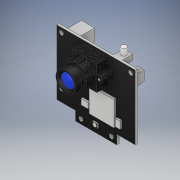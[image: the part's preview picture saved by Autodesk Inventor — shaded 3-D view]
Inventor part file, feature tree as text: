
AUTODESK INVENTOR PART (.ipt)
format: ipt  version: 2017 (Build 210142000, 142)  size: 648,704 bytes
history: native  units: in
note: dims shown in document units (in); Inventor stores cm internally (conversion verified against a paired STEP export)
features: sketch x25, extrude x23, projected_geometry x8, chamfer x5, pattern_linear x4, plane x2, revolve x2, fillet x2, mirror x1, other x1
ambient origin geometry x8: Origin, YZ Plane, XZ Plane, XY Plane, X Axis, Y Axis, Z Axis, Center Point
bodies: Solid1 (feature_tree)
feature tree (73):
  extrude  "Extrusion1"  Depth=1.75in
  extrude  "Extrusion2"  Depth=0.5in
  extrude  "Extrusion3"  Depth=0.25in
  extrude  "Extrusion4"  Depth=0.12in
  plane  "Work Plane1"
  revolve  "Revolution1"  [1 undecoded]
  extrude  "Extrusion5"  Depth=0.125in
  extrude  "Extrusion6"  Depth=0.15in
  extrude  "Extrusion7"  Depth=0.06in TaperAngle=0.0deg
  extrude  "Extrusion8"  Depth=0.175in
  extrude  "Extrusion9"  Depth=0.063in
  extrude  "Extrusion10"  Depth=0.06in
  plane  "Work Plane2"
  mirror  "Mirror1"
  extrude  "Extrusion11"  Depth=0.59in
  extrude  "Extrusion12"  Depth=0.0016in
  chamfer  "Chamfer1"  Distance=0.2598in
  extrude  "Extrusion13"  Depth=0.047in
  chamfer  "Chamfer2"  Distance=0.038in
  pattern_linear  "Rectangular Pattern1"  Spacing1=0.145in  [1 undecoded]
  extrude  "Extrusion14"  Depth=0.407in
  extrude  "Extrusion15"  Depth=0.284in TaperAngle=0.0deg
  fillet  "Fillet1"  Radius=0.1225in
  extrude  "Extrusion16"  Depth=0.127in
  chamfer  "Chamfer3"  Distance=0.135in
  pattern_linear  "Rectangular Pattern3"  Spacing1=0.173in  [1 undecoded]
  pattern_linear  "Rectangular Pattern4"  Spacing1=0.158in  [1 undecoded]
  extrude  "Extrusion17"  Depth=0.3in
  extrude  "Extrusion18"  Depth=0.369in TaperAngle=0.0deg
  chamfer  "Chamfer4"  Distance=0.018in
  pattern_linear  "Rectangular Pattern5"  Spacing1=0.0543in  [1 undecoded]
  extrude  "Extrusion19"  Depth=0.1in TaperAngle=0.0deg
  extrude  "Extrusion20"  Depth=0.35in
  fillet  "Fillet2"  Radius=0.8in
  extrude  "Extrusion21"  Depth=0.184in
  extrude  "Extrusion22"  Depth=0.049in
  revolve  "Revolution2"  [1 undecoded]
  extrude  "Extrusion23"  Depth=0.127in
  chamfer  "Chamfer5"  Distance=0.174in
  sketch  "Sketch1"  dims[d0=2.12in d1=1.75in]
  sketch  "Sketch2"  dims[d2=0.5in d3=0.5in]
  sketch  "Sketch3"  dims[d4=0.25in d5=0.125in]
  projected_geometry  "Projected Loop1"
  sketch  "Sketch4"  dims[d6=0.125in d7=0.12in]
  projected_geometry  "Projected Loop2"
  other  "Work Axis1"
  sketch  "Sketch5"  dims[d8=0.125in d9=0.12in]
  projected_geometry  "Projected Loop3"
  sketch  "Sketch6"  dims[d10=0.32in d11=0.125in]
  sketch  "Sketch7"  dims[d12=0.15in d13=0.15in]
  sketch  "Sketch8"  dims[d14=0.125in d15=0.06in d16=0.0in]
  sketch  "Sketch9"  dims[d17=0.67in d18=0.175in]
  sketch  "Sketch10"  dims[d19=0.964in d20=0.063in]
  sketch  "Sketch11"  dims[d21=0.06in d22=0.335in]
  projected_geometry  "Projected Loop4"
  sketch  "Sketch12"  dims[d23=0.314in d24=0.0in d25=0.59in]
  sketch  "Sketch13"  dims[d26=0.115in d27=0.238in d28=0.0016in]
  projected_geometry  "Projected Loop5"
  sketch  "Sketch14"  dims[d29=0.552in d30=0.2598in d31=0.0in]
  sketch  "Sketch15"  dims[d32=0.0in d33=0.047in]
  projected_geometry  "Projected Loop6"
  sketch  "Sketch16"  dims[d34=0.096in]
  sketch  "Sketch17"  dims[d35=135.0deg]
  projected_geometry  "Projected Loop7"
  sketch  "Sketch18"  dims[d36=0.02in]
  sketch  "Sketch19"  dims[d37=90.0deg]
  sketch  "Sketch20"  dims[d38=0.1111in]
  sketch  "Sketch21"  dims[d39=0.138in]
  sketch  "Sketch22"  dims[d40=0.15in d41=0.038in d42=0.0in]
  sketch  "Sketch23"  dims[d43=0.104in]
  sketch  "Sketch24"  dims[d44=0.0001in d45=0.0in]
  sketch  "Sketch25"  dims[d46=0.245in d47=0.145in d48=0.407in d49=0.284in d50=0.0in d51=0.1225in d52=0.1225in d53=0.135in d54=0.173in d55=0.0in d56=0.158in d57=0.3in d58=0.369in d59=0.0in d60=0.018in d61=0.0543in d62=0.1in d63=0.0in d64=0.35in d65=0.8in d66=0.184in d67=0.049in d68=0.424in d69=0.0in d70=0.04in d71=0.174in d72=0.261in d73=0.0in d74=0.02in d75=0.125in d76=45.0deg d77=0.025in d78=0.05in d79=0.2in d80=0.24in d81=0.0in d82=0.01in d83=0.125in d84=45.0deg d85=1.9685in d87=0.1in d88=0.7874in d90=0.1in d91=0.015in d92=0.24in d93=0.0in d94=0.095in d95=0.193in d96=0.359in d97=0.323in d98=0.147in d99=0.0in d100=0.03in d104=0.05in d105=0.025in d106=0.233in d107=0.0in d108=0.01in d109=0.125in d110=45.0deg d111=0.7874in d113=0.1in d114=1.1811in d116=0.0951in d117=0.2in d118=0.051in d119=0.072in d120=0.0in d121=0.05in d122=0.025in d123=0.293in d124=0.0in d125=0.01in d126=0.125in d127=45.0deg d128=0.7874in d130=0.1in d131=0.205in d132=0.091in d133=0.105in d134=0.2in d135=0.036in d136=0.0in d137=0.135in d138=0.078in d139=0.036in d140=0.0in d141=0.03in d142=0.67in d143=0.19in d144=0.525in d145=0.196in d146=0.363in d147=0.126in d148=0.204in d149=0.15in d150=0.19in d151=0.704in d152=0.503in d153=0.05in d154=0.0in d155=0.235in d156=0.251in d157=0.254in d158=0.409in d159=0.091in d160=0.0in d161=0.118in d162=0.234in d163=90.0deg d164=0.194in d165=0.293in d166=0.012in d167=0.26in d168=0.127in d169=0.0in d170=0.05in d171=0.125in d172=45.0deg]
  projected_geometry  "Projected Loop8"
note: 6 required parameter values undecoded (feature->parameter linkage not recoverable at this tier; creation-order binding heuristic only, values carry confidence <= 0.55)